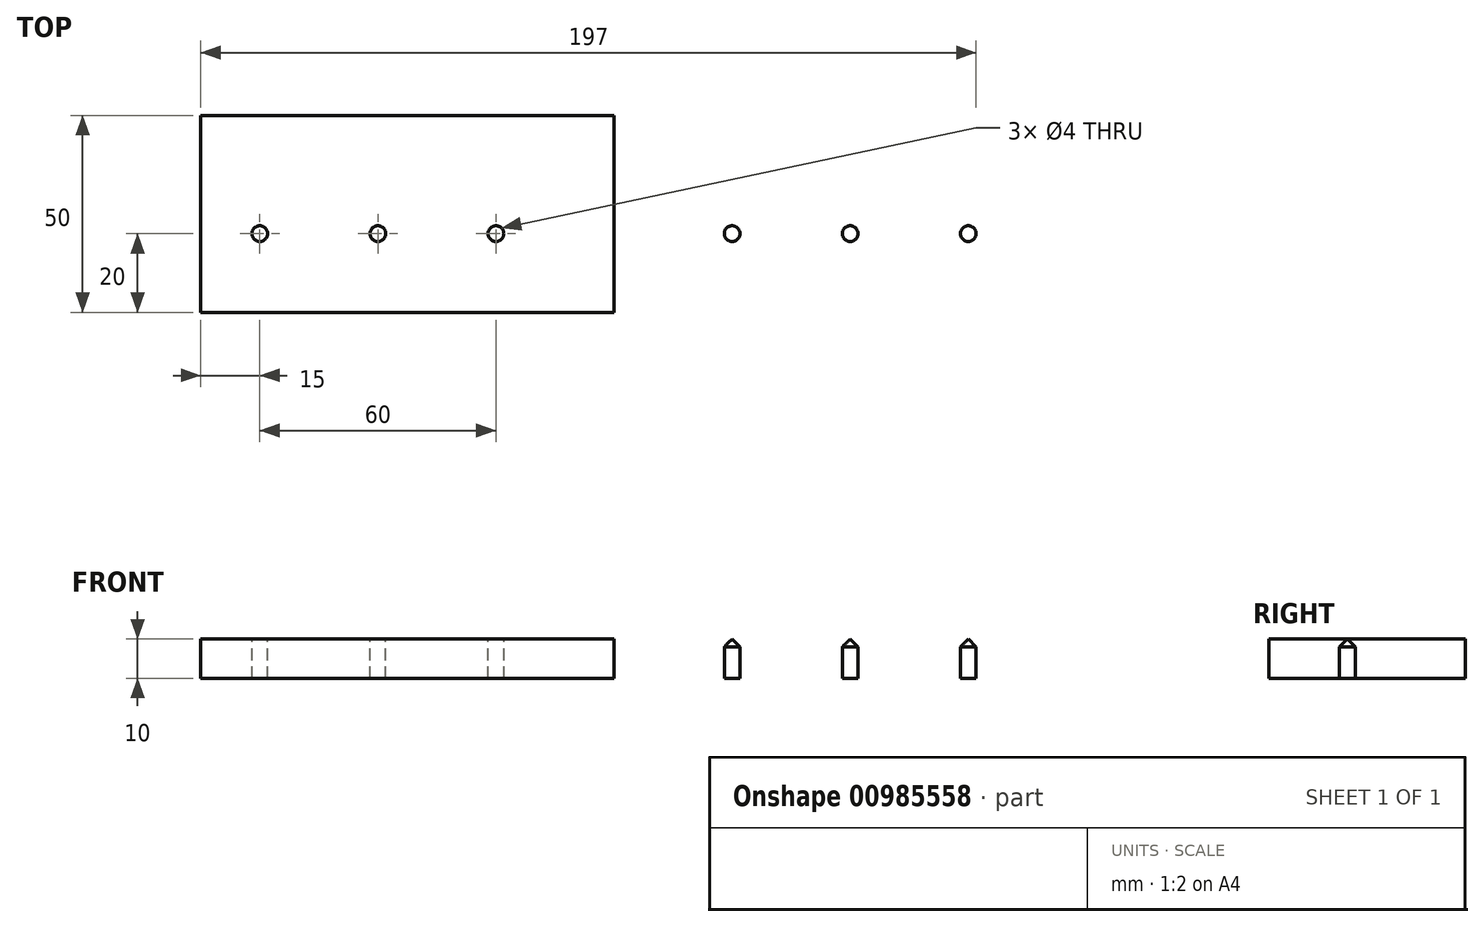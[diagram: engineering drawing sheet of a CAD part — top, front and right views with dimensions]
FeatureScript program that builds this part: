
annotation { "Feature Type Name" : "Feature", "Feature Type Description" : "" }
export const myFeature = defineFeature(function(context is Context, id is Id, definition is map)
    precondition{}
    {
        {
            var Q0;
            Q0=qCreatedBy(makeId("Top.planeOp"),FACE);
            var sketch = newSketch(context, id + "F0", { "sketchPlane" : qUnion([Q0])});
            skLineSegment(sketch, "E0.bottom", {"start": v(105, -25) * mm, "end": v(-105, -25) * mm});
            skLineSegment(sketch, "E0.top", {"start": v(105, 25) * mm, "end": v(-105, 25) * mm});
            skLineSegment(sketch, "E0.left", {"start": v(105, -25) * mm, "end": v(105, 25) * mm});
            skLineSegment(sketch, "E0.right", {"start": v(-105, -25) * mm, "end": v(-105, 25) * mm});
            skPoint(sketch, "E0.middle", {"position": v(0, 0) * mm});
            skSolve(sketch);
        }
        {
            var Q0;
            Q0 = qSketchRegion(id + "F0", true);
            extrude(context, id + "F1", {"entities" : qUnion([Q0]), "depth" : 10 * mm, "offsetDistance" : 25.4 * mm});
        }
        {
            var Q0;
            Q0=makeQuery(id+"F1.opExtrude","CAP_FACE",FACE,{"disambiguationData":[OSD([sQuery(id+"F0.wireOp",EDGE,"E0.bottom"),sQuery(id+"F0.wireOp",EDGE,"E0.top"),sQuery(id+"F0.wireOp",EDGE,"E0.left"),sQuery(id+"F0.wireOp",EDGE,"E0.right")])],"isStart":false});
            var sketch = newSketch(context, id + "F2", { "sketchPlane" : qUnion([Q0])});
            skLineSegment(sketch, "E1", {"start": v(-96.49, -5) * mm, "end": v(158.26, -5) * mm});
            skLineSegment(sketch, "E2", {"start": v(0, 50.94) * mm, "end": v(0, -63.57) * mm});
            skPoint(sketch, "E2.startSnap0", {"position": v(0, 25) * mm});
            skPoint(sketch, "E2.endSnap0", {"position": v(0, -25) * mm});
            skCircle(sketch, "E3", {"center": v(-90, -5) * mm, "radius": 2 * mm});
            skCircle(sketch, "E4", {"center": v(-60, -5) * mm, "radius": 2 * mm});
            skCircle(sketch, "E5", {"center": v(-30, -5) * mm, "radius": 2 * mm});
            skCircle(sketch, "E6", {"center": v(30, -5) * mm, "radius": 2 * mm});
            skCircle(sketch, "E7", {"center": v(60, -5) * mm, "radius": 2 * mm});
            skCircle(sketch, "E8", {"center": v(90, -5) * mm, "radius": 2 * mm});
            skSolve(sketch);
        }
        {
            var Q0;
            {var subQ0=sQuery(id+"F2.wireOp",EDGE,"E3");var subQ1=sQuery(id+"F2.wireOp",EDGE,"E1");var subQ2=makeQuery(id+"F2.imprint","INTERSECT",VERTEX,{"disambiguationData":[OD(0.0)],"derivedFrom":[subQ1,subQ0]});Q0=makeQuery(id+"F2.imprint","IMPRINT",FACE,{"disambiguationData":[TD([[makeQuery(id+"F2.imprint","IMPRINT",EDGE,{"disambiguationData":[TD([[subQ2,-1.0]])],"derivedFrom":subQ1}),1.0]])]});}
            var Q1;
            {var subQ0=sQuery(id+"F2.wireOp",EDGE,"E3");var subQ1=sQuery(id+"F2.wireOp",EDGE,"E1");var subQ2=makeQuery(id+"F2.imprint","INTERSECT",VERTEX,{"disambiguationData":[OD(0.0)],"derivedFrom":[subQ1,subQ0]});Q1=makeQuery(id+"F2.imprint","IMPRINT",FACE,{"disambiguationData":[TD([[makeQuery(id+"F2.imprint","IMPRINT",EDGE,{"disambiguationData":[TD([[subQ2,-1.0]])],"derivedFrom":subQ1}),-1.0]])]});}
            var Q2;
            {var subQ0=sQuery(id+"F2.wireOp",EDGE,"E4");var subQ1=sQuery(id+"F2.wireOp",EDGE,"E1");var subQ2=makeQuery(id+"F2.imprint","INTERSECT",VERTEX,{"disambiguationData":[OD(0.0)],"derivedFrom":[subQ1,subQ0]});Q2=makeQuery(id+"F2.imprint","IMPRINT",FACE,{"disambiguationData":[TD([[makeQuery(id+"F2.imprint","IMPRINT",EDGE,{"disambiguationData":[TD([[subQ2,-1.0]])],"derivedFrom":subQ1}),1.0]])]});}
            var Q3;
            {var subQ0=sQuery(id+"F2.wireOp",EDGE,"E4");var subQ1=sQuery(id+"F2.wireOp",EDGE,"E1");var subQ2=makeQuery(id+"F2.imprint","INTERSECT",VERTEX,{"disambiguationData":[OD(0.0)],"derivedFrom":[subQ1,subQ0]});Q3=makeQuery(id+"F2.imprint","IMPRINT",FACE,{"disambiguationData":[TD([[makeQuery(id+"F2.imprint","IMPRINT",EDGE,{"disambiguationData":[TD([[subQ2,-1.0]])],"derivedFrom":subQ1}),-1.0]])]});}
            var Q4;
            {var subQ0=sQuery(id+"F2.wireOp",EDGE,"E5");var subQ1=sQuery(id+"F2.wireOp",EDGE,"E1");var subQ2=makeQuery(id+"F2.imprint","INTERSECT",VERTEX,{"disambiguationData":[OD(0.0)],"derivedFrom":[subQ1,subQ0]});Q4=makeQuery(id+"F2.imprint","IMPRINT",FACE,{"disambiguationData":[TD([[makeQuery(id+"F2.imprint","IMPRINT",EDGE,{"disambiguationData":[TD([[subQ2,-1.0]])],"derivedFrom":subQ1}),1.0]])]});}
            var Q5;
            {var subQ0=sQuery(id+"F2.wireOp",EDGE,"E5");var subQ1=sQuery(id+"F2.wireOp",EDGE,"E1");var subQ2=makeQuery(id+"F2.imprint","INTERSECT",VERTEX,{"disambiguationData":[OD(0.0)],"derivedFrom":[subQ1,subQ0]});Q5=makeQuery(id+"F2.imprint","IMPRINT",FACE,{"disambiguationData":[TD([[makeQuery(id+"F2.imprint","IMPRINT",EDGE,{"disambiguationData":[TD([[subQ2,-1.0]])],"derivedFrom":subQ1}),-1.0]])]});}
            var Q6;
            {var subQ0=sQuery(id+"F2.wireOp",EDGE,"E6");var subQ1=sQuery(id+"F2.wireOp",EDGE,"E1");var subQ2=makeQuery(id+"F2.imprint","INTERSECT",VERTEX,{"disambiguationData":[OD(0.0)],"derivedFrom":[subQ1,subQ0]});Q6=makeQuery(id+"F2.imprint","IMPRINT",FACE,{"disambiguationData":[TD([[makeQuery(id+"F2.imprint","IMPRINT",EDGE,{"disambiguationData":[TD([[subQ2,-1.0]])],"derivedFrom":subQ1}),1.0]])]});}
            var Q7;
            {var subQ0=sQuery(id+"F2.wireOp",EDGE,"E6");var subQ1=sQuery(id+"F2.wireOp",EDGE,"E1");var subQ2=makeQuery(id+"F2.imprint","INTERSECT",VERTEX,{"disambiguationData":[OD(0.0)],"derivedFrom":[subQ1,subQ0]});Q7=makeQuery(id+"F2.imprint","IMPRINT",FACE,{"disambiguationData":[TD([[makeQuery(id+"F2.imprint","IMPRINT",EDGE,{"disambiguationData":[TD([[subQ2,-1.0]])],"derivedFrom":subQ1}),-1.0]])]});}
            var Q8;
            {var subQ0=sQuery(id+"F2.wireOp",EDGE,"E7");var subQ1=sQuery(id+"F2.wireOp",EDGE,"E1");var subQ2=makeQuery(id+"F2.imprint","INTERSECT",VERTEX,{"disambiguationData":[OD(0.0)],"derivedFrom":[subQ1,subQ0]});Q8=makeQuery(id+"F2.imprint","IMPRINT",FACE,{"disambiguationData":[TD([[makeQuery(id+"F2.imprint","IMPRINT",EDGE,{"disambiguationData":[TD([[subQ2,-1.0]])],"derivedFrom":subQ1}),1.0]])]});}
            var Q9;
            {var subQ0=sQuery(id+"F2.wireOp",EDGE,"E7");var subQ1=sQuery(id+"F2.wireOp",EDGE,"E1");var subQ2=makeQuery(id+"F2.imprint","INTERSECT",VERTEX,{"disambiguationData":[OD(0.0)],"derivedFrom":[subQ1,subQ0]});Q9=makeQuery(id+"F2.imprint","IMPRINT",FACE,{"disambiguationData":[TD([[makeQuery(id+"F2.imprint","IMPRINT",EDGE,{"disambiguationData":[TD([[subQ2,-1.0]])],"derivedFrom":subQ1}),-1.0]])]});}
            var Q10;
            {var subQ0=sQuery(id+"F2.wireOp",EDGE,"E8");var subQ1=sQuery(id+"F2.wireOp",EDGE,"E1");var subQ2=makeQuery(id+"F2.imprint","INTERSECT",VERTEX,{"disambiguationData":[OD(0.0)],"derivedFrom":[subQ1,subQ0]});Q10=makeQuery(id+"F2.imprint","IMPRINT",FACE,{"disambiguationData":[TD([[makeQuery(id+"F2.imprint","IMPRINT",EDGE,{"disambiguationData":[TD([[subQ2,-1.0]])],"derivedFrom":subQ1}),1.0]])]});}
            var Q11;
            {var subQ0=sQuery(id+"F2.wireOp",EDGE,"E8");var subQ1=sQuery(id+"F2.wireOp",EDGE,"E1");var subQ2=makeQuery(id+"F2.imprint","INTERSECT",VERTEX,{"disambiguationData":[OD(0.0)],"derivedFrom":[subQ1,subQ0]});Q11=makeQuery(id+"F2.imprint","IMPRINT",FACE,{"disambiguationData":[TD([[makeQuery(id+"F2.imprint","IMPRINT",EDGE,{"disambiguationData":[TD([[subQ2,-1.0]])],"derivedFrom":subQ1}),-1.0]])]});}
            extrude(context, id + "F3", {"entities" : qUnion([Q0, Q1, Q2, Q3, Q4, Q5, Q6, Q7, Q8, Q9, Q10, Q11]), "operationType" : NewBodyOperationType.REMOVE, "endBound" : BoundingType.THROUGH_ALL, "oppositeDirection" : true, "depth" : 25.4 * mm, "offsetDistance" : 25.4 * mm});
        }
        {
            var Q0;
            Q0=makeQuery(id+"F3.boolean.opBoolean","COPY",EDGE,{"derivedFrom":makeQuery(id+"F3.opExtrude","CAP_EDGE",EDGE,{"disambiguationData":[OSD([sQuery(id+"F2.wireOp",EDGE,"E3")])],"isStart":true})});
            var Q1;
            Q1=makeQuery(id+"F3.boolean.opBoolean","COPY",EDGE,{"derivedFrom":makeQuery(id+"F3.opExtrude","CAP_EDGE",EDGE,{"disambiguationData":[OSD([sQuery(id+"F2.wireOp",EDGE,"E4")])],"isStart":true})});
            var Q2;
            Q2=makeQuery(id+"F3.boolean.opBoolean","COPY",EDGE,{"derivedFrom":makeQuery(id+"F3.opExtrude","CAP_EDGE",EDGE,{"disambiguationData":[OSD([sQuery(id+"F2.wireOp",EDGE,"E5")])],"isStart":true})});
            var Q3;
            Q3=makeQuery(id+"F3.boolean.opBoolean","COPY",EDGE,{"derivedFrom":makeQuery(id+"F3.opExtrude","CAP_EDGE",EDGE,{"disambiguationData":[OSD([sQuery(id+"F2.wireOp",EDGE,"E6")])],"isStart":true})});
            var Q4;
            Q4=makeQuery(id+"F3.boolean.opBoolean","COPY",EDGE,{"derivedFrom":makeQuery(id+"F3.opExtrude","CAP_EDGE",EDGE,{"disambiguationData":[OSD([sQuery(id+"F2.wireOp",EDGE,"E7")])],"isStart":true})});
            var Q5;
            Q5=makeQuery(id+"F3.boolean.opBoolean","COPY",EDGE,{"derivedFrom":makeQuery(id+"F3.opExtrude","CAP_EDGE",EDGE,{"disambiguationData":[OSD([sQuery(id+"F2.wireOp",EDGE,"E8")])],"isStart":true})});
            chamfer(context, id + "F4", {"entities" : qUnion([Q0, Q1, Q2, Q3, Q4, Q5]), "width" : 2 * mm, "tangentPropagation" : true});
        }
    });
